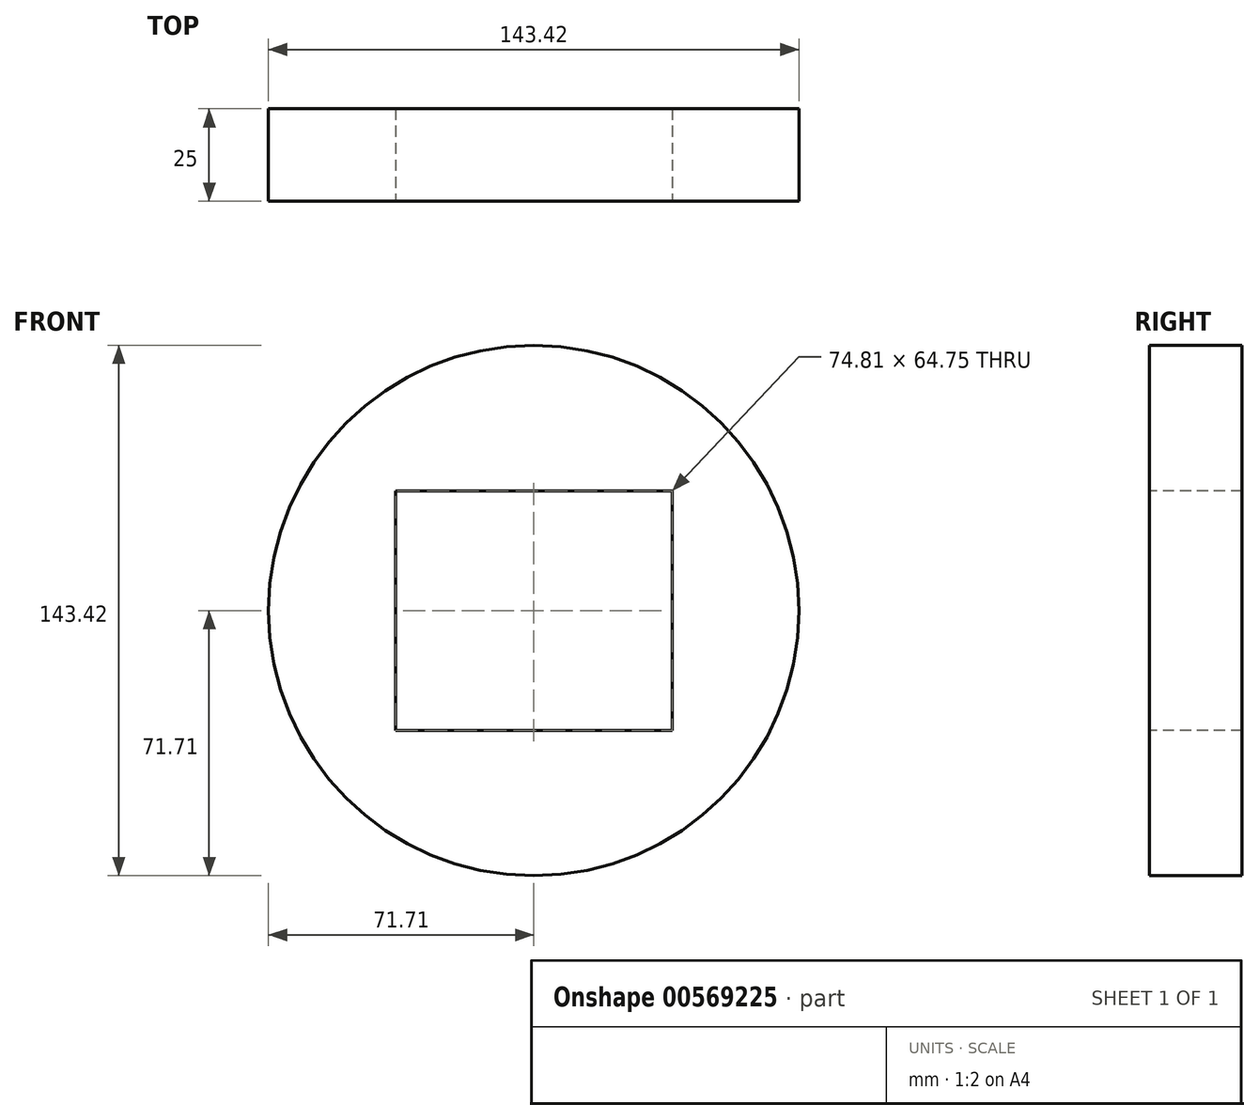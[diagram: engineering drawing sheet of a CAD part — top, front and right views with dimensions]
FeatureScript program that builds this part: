
annotation { "Feature Type Name" : "Feature", "Feature Type Description" : "" }
export const myFeature = defineFeature(function(context is Context, id is Id, definition is map)
    precondition{}
    {
        {
            var Q0;
            Q0=qCreatedBy(makeId("Front.planeOp"),FACE);
            var sketch = newSketch(context, id + "F0", { "sketchPlane" : qUnion([Q0])});
            skCircle(sketch, "E0", {"center": v(0, 0) * mm, "radius": 71.7 * mm});
            skSolve(sketch);
        }
        {
            var Q0;
            Q0=makeQuery(id+"F0.imprint","IMPRINT",FACE,{"disambiguationData":[TD([[makeQuery(id+"F0.imprint","IMPRINT",EDGE,{"derivedFrom":sQuery(id+"F0.wireOp",EDGE,"E0")}),1.0]])]});
            var sketch = newSketch(context, id + "F1", { "sketchPlane" : qUnion([Q0])});
            skLineSegment(sketch, "E1.bottom", {"start": v(37.4, -32.38) * mm, "end": v(-37.4, -32.38) * mm});
            skLineSegment(sketch, "E1.top", {"start": v(37.4, 32.38) * mm, "end": v(-37.4, 32.38) * mm});
            skLineSegment(sketch, "E1.left", {"start": v(37.4, -32.38) * mm, "end": v(37.4, 32.38) * mm});
            skLineSegment(sketch, "E1.right", {"start": v(-37.4, -32.38) * mm, "end": v(-37.4, 32.38) * mm});
            skPoint(sketch, "E1.middle", {"position": v(0, 0) * mm});
            skSolve(sketch);
        }
        {
            var Q0;
            Q0 = qSketchRegion(id + "F0", true);
            extrude(context, id + "F2", {"entities" : qUnion([Q0]), "depth" : 25 * mm, "offsetDistance" : 25 * mm});
        }
        {
            var Q0;
            Q0 = qSketchRegion(id + "F1", true);
            extrude(context, id + "F3", {"entities" : qUnion([Q0]), "operationType" : NewBodyOperationType.REMOVE, "endBound" : BoundingType.SYMMETRIC, "oppositeDirection" : true, "depth" : 50 * mm, "offsetDistance" : 25 * mm});
        }
    });
